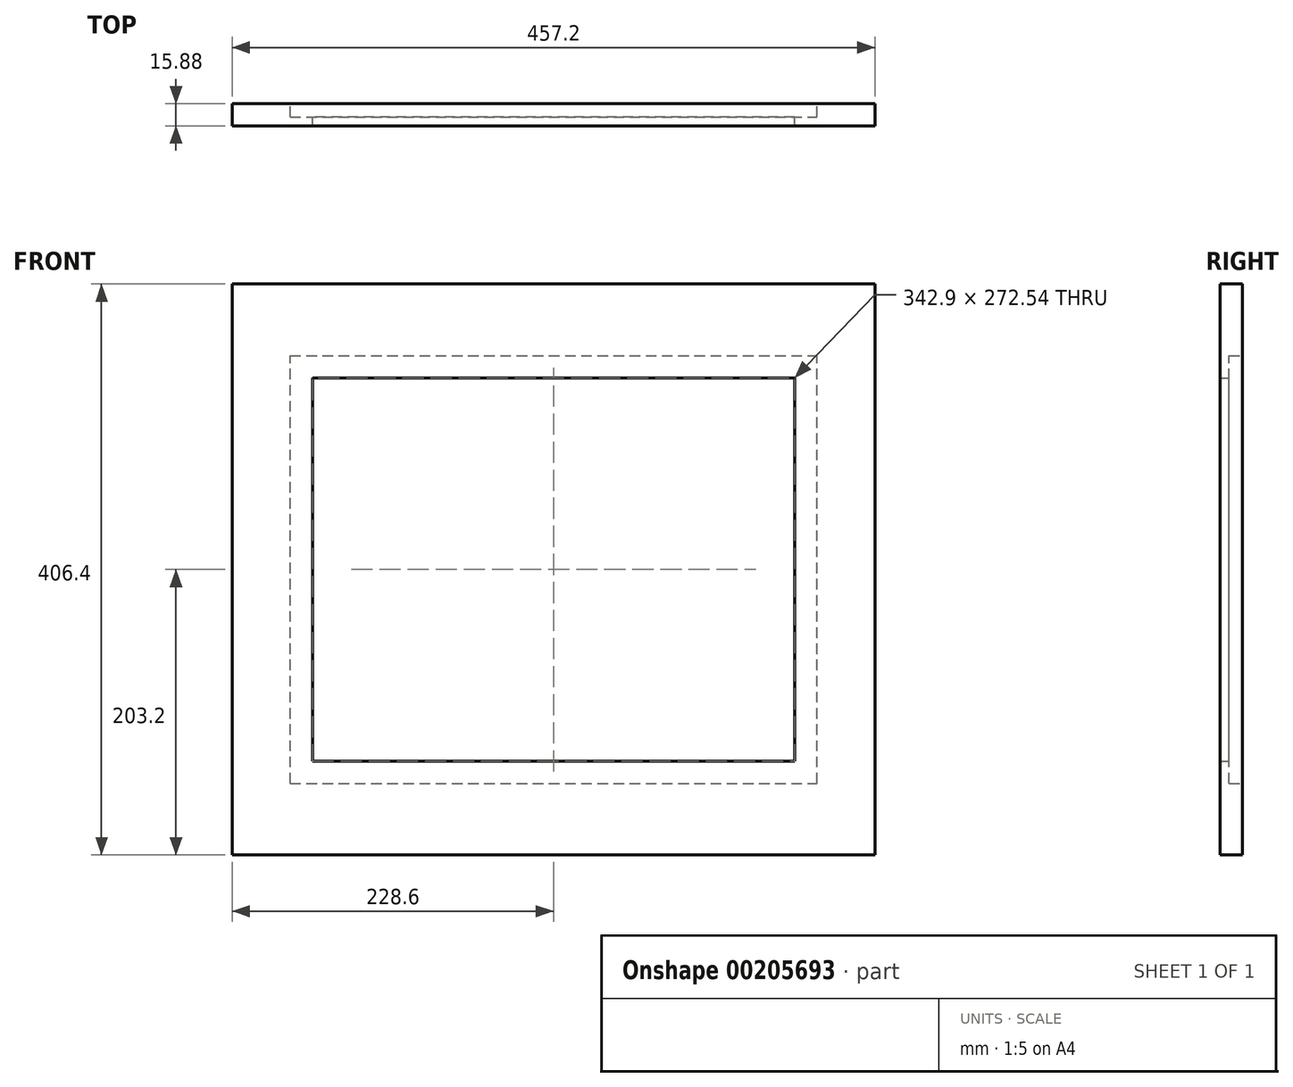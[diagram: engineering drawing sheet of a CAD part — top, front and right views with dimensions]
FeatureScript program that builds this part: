
annotation { "Feature Type Name" : "Feature", "Feature Type Description" : "" }
export const myFeature = defineFeature(function(context is Context, id is Id, definition is map)
    precondition{}
    {
        {
            var Q0;
            Q0=qCreatedBy(makeId("Front.planeOp"),FACE);
            var sketch = newSketch(context, id + "F0", { "sketchPlane" : qUnion([Q0])});
            skLineSegment(sketch, "E0.bottom", {"start": v(171.45, -136.27) * mm, "end": v(-171.45, -136.27) * mm});
            skLineSegment(sketch, "E0.top", {"start": v(171.45, 136.27) * mm, "end": v(-171.45, 136.27) * mm});
            skLineSegment(sketch, "E0.left", {"start": v(171.45, -136.27) * mm, "end": v(171.45, 136.27) * mm});
            skLineSegment(sketch, "E0.right", {"start": v(-171.45, -136.27) * mm, "end": v(-171.45, 136.27) * mm});
            skPoint(sketch, "E0.middle", {"position": v(0, 0) * mm});
            skLineSegment(sketch, "E1.bottom", {"start": v(228.6, -203.2) * mm, "end": v(-228.6, -203.2) * mm});
            skLineSegment(sketch, "E1.top", {"start": v(228.6, 203.2) * mm, "end": v(-228.6, 203.2) * mm});
            skLineSegment(sketch, "E1.left", {"start": v(228.6, -203.2) * mm, "end": v(228.6, 203.2) * mm});
            skLineSegment(sketch, "E1.right", {"start": v(-228.6, -203.2) * mm, "end": v(-228.6, 203.2) * mm});
            skSolve(sketch);
        }
        {
            var Q0;
            Q0=makeQuery(id+"F0.imprint","IMPRINT",FACE,{"disambiguationData":[TD([[makeQuery(id+"F0.imprint","IMPRINT",EDGE,{"derivedFrom":sQuery(id+"F0.wireOp",EDGE,"E0.bottom")}),1.0]])]});
            extrude(context, id + "F1", {"entities" : qUnion([Q0]), "depth" : 15.88 * mm});
        }
        {
            var Q0;
            Q0=makeQuery(id+"F1.opExtrude","CAP_FACE",FACE,{"disambiguationData":[OSD([sQuery(id+"F0.wireOp",EDGE,"E0.bottom"),sQuery(id+"F0.wireOp",EDGE,"E0.top"),sQuery(id+"F0.wireOp",EDGE,"E0.left"),sQuery(id+"F0.wireOp",EDGE,"E0.right"),sQuery(id+"F0.wireOp",EDGE,"E1.bottom"),sQuery(id+"F0.wireOp",EDGE,"E1.top"),sQuery(id+"F0.wireOp",EDGE,"E1.left"),sQuery(id+"F0.wireOp",EDGE,"E1.right")])],"isStart":true});
            var sketch = newSketch(context, id + "F2", { "sketchPlane" : qUnion([Q0])});
            skLineSegment(sketch, "E2.bottom", {"start": v(187.33, -152.15) * mm, "end": v(-187.33, -152.15) * mm});
            skLineSegment(sketch, "E2.top", {"start": v(187.33, 152.15) * mm, "end": v(-187.33, 152.15) * mm});
            skLineSegment(sketch, "E2.left", {"start": v(187.33, -152.15) * mm, "end": v(187.33, 152.15) * mm});
            skLineSegment(sketch, "E2.right", {"start": v(-187.33, -152.15) * mm, "end": v(-187.33, 152.15) * mm});
            skPoint(sketch, "E2.middle", {"position": v(0, 0) * mm});
            skSolve(sketch);
        }
        {
            var Q0;
            Q0=makeQuery(id+"F2.imprint","IMPRINT",FACE,{"disambiguationData":[TD([[makeQuery(id+"F2.imprint","IMPRINT",EDGE,{"derivedFrom":sQuery(id+"F2.wireOp",EDGE,"E2.bottom")}),-1.0]])]});
            extrude(context, id + "F3", {"entities" : qUnion([Q0]), "operationType" : NewBodyOperationType.REMOVE, "oppositeDirection" : true, "depth" : 9.52 * mm});
        }
    });
